# Revit family: КАМ_Eng
name_source: partatom
category: Mechanical Equipment
units: mm (PartAtom-declared; Revit-internal decimal feet)

## family parameters
Always vertical = Yes
Classification = None
Cut with Voids When Loaded = No
Part Type = Normal
Room Calculation Point = No
Round Connector Dimension = Use Diameter
Shared = No
Work Plane-Based = No

## types (7) — shared parameters
00_20_Manufacturer = Vents
00_20_Name = Chimney centrifugal fan
Casing Material = Steel, galvanized
Frequency = 50 Hz
KFK = Yes
Load Classification = HVAC
Maintenance zone material = <By Category>
Manufacturer = Vents
Number of Fase = 1
P = 50 mm  [stored 0.164042 ft]
URL = https://ventilation-system.com
Voltage = 230 V
zero-valued in all types: Default Elevation

## per-type parameters (varying)
- KAM 125: Amperage=1 A; Apparent Load=186 VA; B=245 mm  [stored 0.803806 ft]; D=125 mm  [stored 0.410105 ft]; Diameter=125 mm  [stored 0.410105 ft]; Dy=115 mm  [stored 0.377297 ft]; H=350 mm  [stored 1.14829 ft]; H1=300 mm; Height=610 mm  [stored 2.00131 ft]; Hn=250 mm  [stored 0.82021 ft]; Hv=610 mm  [stored 2.00131 ft]; KAM from KFK=8.50 kg; KFK_O=KFK : 125; L=260 mm  [stored 0.853018 ft]; Length=260 mm  [stored 0.853018 ft]; Lk=115 mm  [stored 0.377297 ft]; Maximum Air Flow=400.0 m³/h; Power=108 W; Sound pressure level at 3 m distance=42 dBA; Weight=8.50 kg; Weight  KAM=5.82 kg; Width=295 mm  [stored 0.967848 ft]; b=123 mm; b2=113 mm; h1=83 mm  [stored 0.27231 ft]; l=210 mm  [stored 0.688976 ft]; l1=105 mm  [stored 0.344488 ft]; l2=95 mm
- KAM 160: Amperage=1 A; Apparent Load=198 VA; B=285 mm  [stored 0.935039 ft]; D=160 mm  [stored 0.524934 ft]; Diameter=160 mm  [stored 0.524934 ft]; Dy=150 mm; H=350 mm  [stored 1.14829 ft]; H1=300 mm; Height=650 mm  [stored 2.13255 ft]; Hn=250 mm  [stored 0.82021 ft]; Hv=650 mm  [stored 2.13255 ft]; KAM from KFK=9.70 kg; KFK_O=KFK : 160; L=300 mm; Length=300 mm; Lk=135 mm  [stored 0.442913 ft]; Maximum Air Flow=540.0 m³/h; Power=116 W; Sound pressure level at 3 m distance=42 dBA; Weight=9.70 kg; Weight  KAM=6.90 kg; Width=335 mm; b=143 mm; b2=133 mm; h1=100 mm  [stored 0.328084 ft]; l=250 mm  [stored 0.82021 ft]; l1=125 mm  [stored 0.410105 ft]; l2=115 mm  [stored 0.377297 ft]
- KAM 150: Amperage=1 A; Apparent Load=193 VA; B=285 mm  [stored 0.935039 ft]; D=150 mm; Diameter=150 mm; Dy=140 mm  [stored 0.459318 ft]; H=350 mm  [stored 1.14829 ft]; H1=300 mm; Height=650 mm  [stored 2.13255 ft]; Hn=250 mm  [stored 0.82021 ft]; Hv=650 mm  [stored 2.13255 ft]; KAM from KFK=9.70 kg; KFK_O=KFK : 150; L=300 mm; Length=300 mm; Lk=135 mm  [stored 0.442913 ft]; Maximum Air Flow=520.0 m³/h; Power=115 W; Sound pressure level at 3 m distance=42 dBA; Weight=9.70 kg; Weight  KAM=6.90 kg; Width=335 mm; b=143 mm; b2=133 mm; h1=95 mm; l=250 mm  [stored 0.82021 ft]; l1=125 mm  [stored 0.410105 ft]; l2=115 mm  [stored 0.377297 ft]
- KAM 125 Eco: Amperage=0 A; Apparent Load=32 VA; B=245 mm  [stored 0.803806 ft]; D=125 mm  [stored 0.410105 ft]; Diameter=125 mm  [stored 0.410105 ft]; Dy=115 mm  [stored 0.377297 ft]; H=320 mm  [stored 1.04987 ft]; H1=270 mm  [stored 0.885827 ft]; Height=550 mm; Hn=220 mm  [stored 0.721785 ft]; Hv=550 mm; KAM from KFK=9.40 kg; KFK_O=KFK : 125; L=260 mm  [stored 0.853018 ft]; Length=260 mm  [stored 0.853018 ft]; Lk=115 mm  [stored 0.377297 ft]; Maximum Air Flow=350.0 m³/h; Power=32 W; Sound pressure level at 3 m distance=37 dBA; Weight=9.40 kg; Weight  KAM=5.82 kg; Width=295 mm  [stored 0.967848 ft]; b=123 mm; b2=113 mm; h1=83 mm  [stored 0.27231 ft]; l=210 mm  [stored 0.688976 ft]; l1=105 mm  [stored 0.344488 ft]; l2=95 mm
- KAM 150 Eco: Amperage=0 A; Apparent Load=44 VA; B=285 mm  [stored 0.935039 ft]; D=150 mm; Diameter=150 mm; Dy=140 mm  [stored 0.459318 ft]; H=320 mm  [stored 1.04987 ft]; H1=270 mm  [stored 0.885827 ft]; Height=590 mm  [stored 1.9357 ft]; Hn=220 mm  [stored 0.721785 ft]; Hv=590 mm  [stored 1.9357 ft]; KAM from KFK=10.80 kg; KFK_O=KFK : 150 Eco; L=300 mm; Length=300 mm; Lk=135 mm  [stored 0.442913 ft]; Maximum Air Flow=450.0 m³/h; Power=43 W; Sound pressure level at 3 m distance=39 dBA; Weight=10.80 kg; Weight  KAM=6.90 kg; Width=335 mm; b=143 mm; b2=133 mm; h1=95 mm; l=250 mm  [stored 0.82021 ft]; l1=125 mm  [stored 0.410105 ft]; l2=115 mm  [stored 0.377297 ft]
- KAM 160 Eco: Amperage=0 A; Apparent Load=44 VA; B=285 mm  [stored 0.935039 ft]; D=160 mm  [stored 0.524934 ft]; Diameter=160 mm  [stored 0.524934 ft]; Dy=150 mm; H=320 mm  [stored 1.04987 ft]; H1=270 mm  [stored 0.885827 ft]; Height=590 mm  [stored 1.9357 ft]; Hn=220 mm  [stored 0.721785 ft]; Hv=590 mm  [stored 1.9357 ft]; KAM from KFK=10.80 kg; KFK_O=KFK : 160 Eco; L=300 mm; Length=300 mm; Lk=135 mm  [stored 0.442913 ft]; Maximum Air Flow=470.0 m³/h; Power=44 W; Sound pressure level at 3 m distance=39 dBA; Weight=10.80 kg; Weight  KAM=6.90 kg; Width=335 mm; b=143 mm; b2=133 mm; h1=100 mm  [stored 0.328084 ft]; l=250 mm  [stored 0.82021 ft]; l1=125 mm  [stored 0.410105 ft]; l2=115 mm  [stored 0.377297 ft]
- KAM 150 Eco max: Amperage=1 A; Apparent Load=117 VA; B=285 mm  [stored 0.935039 ft]; D=150 mm; Diameter=150 mm; Dy=140 mm  [stored 0.459318 ft]; H=320 mm  [stored 1.04987 ft]; H1=270 mm  [stored 0.885827 ft]; Height=590 mm  [stored 1.9357 ft]; Hn=220 mm  [stored 0.721785 ft]; Hv=590 mm  [stored 1.9357 ft]; KAM from KFK=10.80 kg; KFK_O=KFK : 150 Eco max; L=300 mm; Length=300 mm; Lk=135 mm  [stored 0.442913 ft]; Maximum Air Flow=613.0 m³/h; Power=115 W; Sound pressure level at 3 m distance=45 dBA; Weight=10.80 kg; Weight  KAM=6.90 kg; Width=335 mm; b=143 mm; b2=133 mm; h1=95 mm; l=250 mm  [stored 0.82021 ft]; l1=125 mm  [stored 0.410105 ft]; l2=115 mm  [stored 0.377297 ft]

note: column(s) folded — value = type name in every type: 00_20_Type

note: [stored X ft] marks values corroborated as IEEE doubles in the binary element streams (Revit-internal decimal feet)
